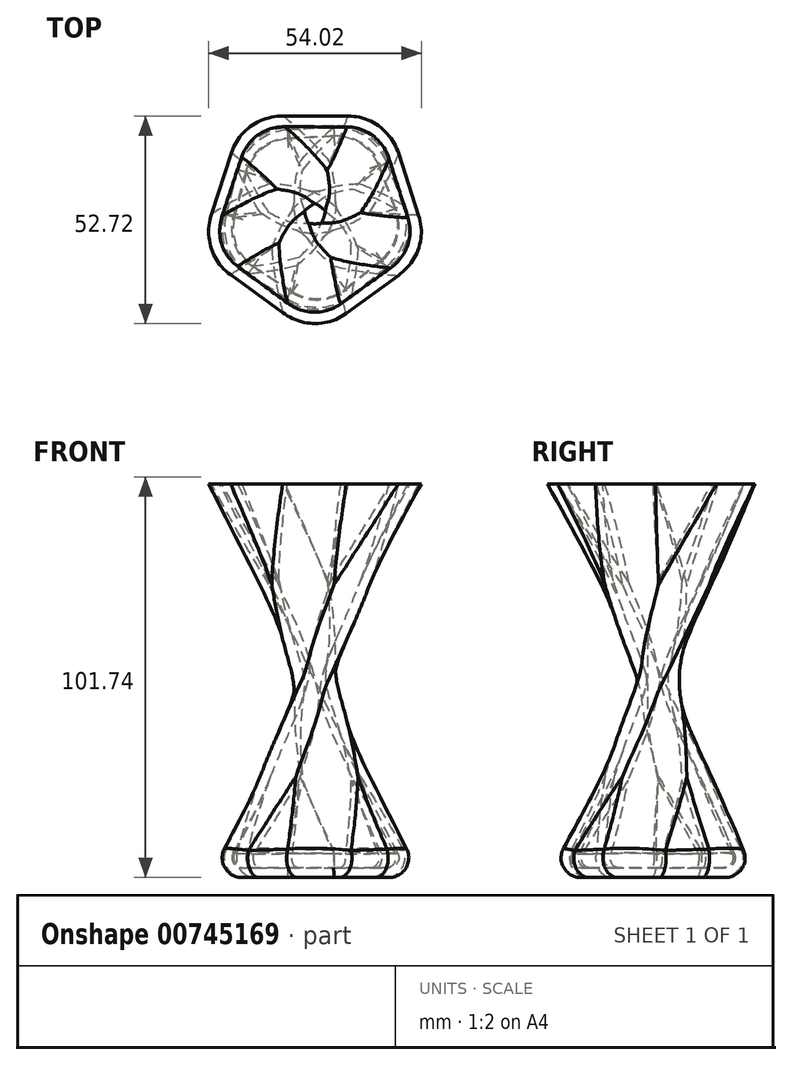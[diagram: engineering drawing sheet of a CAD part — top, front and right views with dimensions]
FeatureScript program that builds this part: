
annotation { "Feature Type Name" : "Feature", "Feature Type Description" : "" }
export const myFeature = defineFeature(function(context is Context, id is Id, definition is map)
    precondition{}
    {
        {
            var Q0;
            Q0=qCreatedBy(makeId("Top.planeOp"),FACE);
            cPlane(context, id + "F0", {"entities" : qUnion([Q0]), "cplaneType" : CPlaneType.OFFSET, "offset" : 100 * mm, "width" : 150 * mm, "height" : 150 * mm});
        }
        {
            var Q0;
            Q0=qCreatedBy(makeId("Top.planeOp"),FACE);
            var sketch = newSketch(context, id + "F1", { "sketchPlane" : qUnion([Q0])});
            skCircle(sketch, "E0.cCircle", {"center": v(0, 0) * mm, "radius": 25 * mm, "construction": true});
            skLineSegment(sketch, "E0.0", {"start": v(-18.16, 25) * mm, "end": v(18.16, 25) * mm});
            skLineSegment(sketch, "E0.1", {"start": v(18.16, 25) * mm, "end": v(29.39, -9.55) * mm});
            skLineSegment(sketch, "E0.2", {"start": v(29.39, -9.55) * mm, "end": v(0, -30.9) * mm});
            skLineSegment(sketch, "E0.3", {"start": v(0, -30.9) * mm, "end": v(-29.39, -9.55) * mm});
            skLineSegment(sketch, "E0.4", {"start": v(-29.39, -9.55) * mm, "end": v(-18.16, 25) * mm});
            skPoint(sketch, "E0.0.midPoint", {"position": v(0, 25) * mm});
            skSolve(sketch);
        }
        {
            var Q0;
            Q0=qCreatedBy(id+"F0.planeOp",FACE);
            var sketch = newSketch(context, id + "F2", { "sketchPlane" : qUnion([Q0])});
            skLineSegment(sketch, "E1.0", {"start": v(-18.16, 25) * mm, "end": v(18.16, 25) * mm});
            skLineSegment(sketch, "E1.1", {"start": v(-29.39, -9.55) * mm, "end": v(-18.16, 25) * mm});
            skLineSegment(sketch, "E1.2", {"start": v(0, -30.9) * mm, "end": v(-29.39, -9.55) * mm});
            skLineSegment(sketch, "E1.3", {"start": v(29.39, -9.55) * mm, "end": v(0, -30.9) * mm});
            skLineSegment(sketch, "E1.4", {"start": v(18.16, 25) * mm, "end": v(29.39, -9.55) * mm});
            skSolve(sketch);
        }
        {
            var Q0;
            Q0 = qSketchRegion(id + "F1", true);
            var Q1;
            Q1 = qSketchRegion(id + "F2", true);
            var Q2;
            Q2=sQuery(id+"F2.wireOp",VERTEX,"E1.2.end");
            var Q3;
            Q3=sQuery(id+"F1.wireOp",VERTEX,"E0.1.start");
            loft(context, id + "F3", {"sheetProfilesArray" : [{ "sheetProfileEntities" : qUnion([Q0]) }, { "sheetProfileEntities" : qUnion([Q1]) }], "matchConnections" : true, "connections" : [{ "connectionEntities" : qUnion([Q2, Q3]), "connectionEdgeQueries" : qUnion([]), "connectionEdgeParameters" : [] }]});
        }
        {
            var Q0;
            Q0=makeQuery(id+"F3.opLoft","SWEPT_EDGE",EDGE,{"disambiguationData":[OSD([sQuery(id+"F1.wireOp",EDGE,"E0.0"),sQuery(id+"F1.wireOp",EDGE,"E0.1"),sQuery(id+"F2.wireOp",EDGE,"E1.1"),sQuery(id+"F2.wireOp",EDGE,"E1.2")])]});
            var Q1;
            Q1=makeQuery(id+"F3.opLoft","SWEPT_EDGE",EDGE,{"disambiguationData":[OSD([sQuery(id+"F1.wireOp",EDGE,"E0.1"),sQuery(id+"F1.wireOp",EDGE,"E0.2"),sQuery(id+"F2.wireOp",EDGE,"E1.0"),sQuery(id+"F2.wireOp",EDGE,"E1.1")])]});
            var Q2;
            Q2=makeQuery(id+"F3.opLoft","SWEPT_EDGE",EDGE,{"disambiguationData":[OSD([sQuery(id+"F1.wireOp",EDGE,"E0.2"),sQuery(id+"F1.wireOp",EDGE,"E0.3"),sQuery(id+"F2.wireOp",EDGE,"E1.0"),sQuery(id+"F2.wireOp",EDGE,"E1.4")])]});
            var Q3;
            Q3=makeQuery(id+"F3.opLoft","SWEPT_EDGE",EDGE,{"disambiguationData":[OSD([sQuery(id+"F1.wireOp",EDGE,"E0.3"),sQuery(id+"F1.wireOp",EDGE,"E0.4"),sQuery(id+"F2.wireOp",EDGE,"E1.3"),sQuery(id+"F2.wireOp",EDGE,"E1.4")])]});
            var Q4;
            Q4=makeQuery(id+"F3.opLoft","SWEPT_EDGE",EDGE,{"disambiguationData":[OSD([sQuery(id+"F1.wireOp",EDGE,"E0.0"),sQuery(id+"F1.wireOp",EDGE,"E0.4"),sQuery(id+"F2.wireOp",EDGE,"E1.2"),sQuery(id+"F2.wireOp",EDGE,"E1.3")])]});
            fillet(context, id + "F4", {"entities" : qUnion([Q0, Q1, Q2, Q3, Q4]), "radius" : 15 * mm, "tangentPropagation" : true, "allowEdgeOverflow" : false});
        }
        {
            var Q0;
            {var subQ0=sQuery(id+"F1.wireOp",EDGE,"E0.3");var subQ1=sQuery(id+"F1.wireOp",EDGE,"E0.4");Q0=makeQuery(id+"F4.opFillet","BLEND_EDGE",EDGE,{"blendedFrom":[makeQuery(id+"F3.opLoft","SWEPT_EDGE",EDGE,{"disambiguationData":[OSD([subQ0,subQ1,sQuery(id+"F2.wireOp",EDGE,"E1.3"),sQuery(id+"F2.wireOp",EDGE,"E1.4")])]}),makeQuery(id+"F3.opLoft","CAP_FACE",FACE,{"disambiguationData":[OSD([makeQuery(id+"F1.imprint","IMPRINT",FACE,{"disambiguationData":[TD([[makeQuery(id+"F1.imprint","IMPRINT",EDGE,{"derivedFrom":sQuery(id+"F1.wireOp",EDGE,"E0.0")}),-1.0]])]})])],"isStart":true})],"blendedInto":[makeQuery(id+"F3.opLoft","CAP_FACE",FACE,{"disambiguationData":[OSD([makeQuery(id+"F1.imprint","IMPRINT",FACE,{"disambiguationData":[TD([[makeQuery(id+"F1.imprint","IMPRINT",EDGE,{"derivedFrom":sQuery(id+"F1.wireOp",EDGE,"E0.0")}),-1.0]])]})])],"isStart":true})]});}
            fillet(context, id + "F5", {"entities" : qUnion([Q0]), "radius" : 5 * mm, "tangentPropagation" : true, "allowEdgeOverflow" : false});
        }
        {
            var Q0;
            Q0=makeQuery(id+"F3.opLoft","CAP_FACE",FACE,{"disambiguationData":[OSD([makeQuery(id+"F2.imprint","IMPRINT",FACE,{"disambiguationData":[TD([[makeQuery(id+"F2.imprint","IMPRINT",EDGE,{"derivedFrom":sQuery(id+"F2.wireOp",EDGE,"E1.0")}),-1.0]])]})])],"isStart":true});
            shell(context, id + "F6", {"entities" : qUnion([Q0]), "thickness" : 2.5 * mm});
        }
    });
